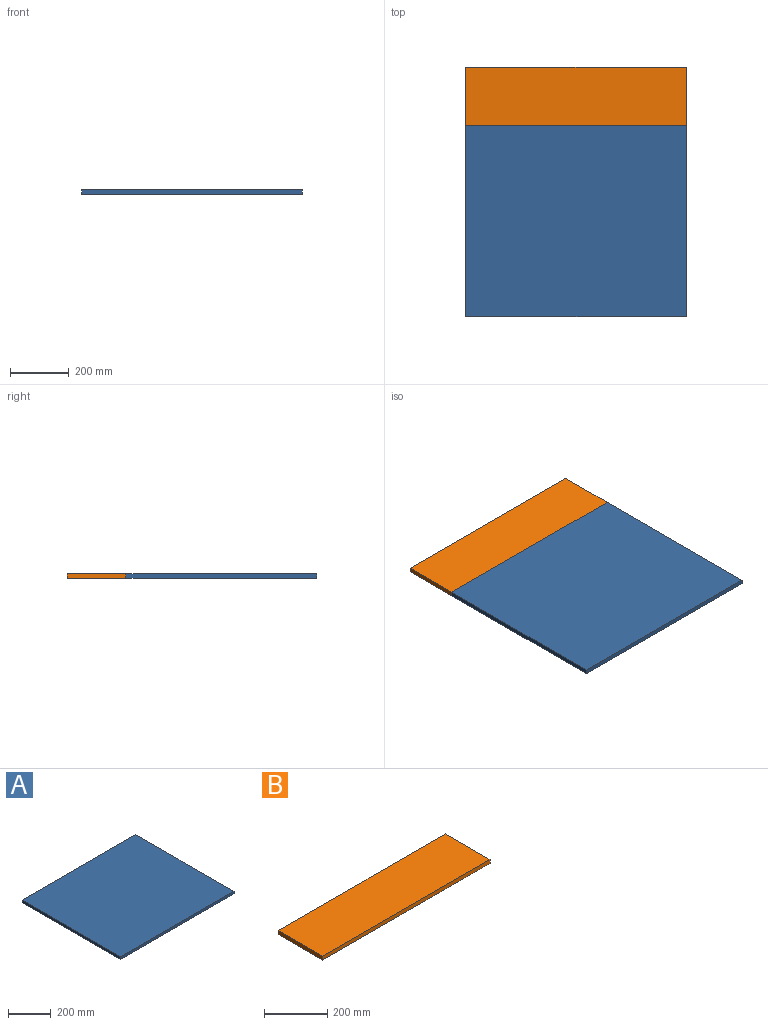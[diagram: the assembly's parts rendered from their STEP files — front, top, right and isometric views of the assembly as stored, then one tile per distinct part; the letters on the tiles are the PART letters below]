
ASSEMBLY  parts=2 mates=1
PART A: 6 faces, bbox 750x650x15 mm
  f0: plane 750x15mm, normal (0,1,0), area 11250mm2, adj f1,f3,f4,f5
  f1: plane 650x15mm, normal (-1,0,0), area 9750mm2, adj f0,f2,f4,f5
  f2: plane 750x15mm, normal (0,-1,0), area 11250mm2, adj f1,f3,f4,f5
  f3: plane 650x15mm, normal (1,0,0), area 9750mm2, adj f0,f2,f4,f5
  f4: plane 750x650mm, normal (0,0,1), area 487500mm2, adj f0,f1,f2,f3
  f5: plane 750x650mm, normal (0,0,-1), area 487500mm2, adj f0,f1,f2,f3
PART B: 6 faces, bbox 750x200x15 mm
  f0: plane 750x15mm, normal (0,1,0), area 11250mm2, adj f1,f3,f4,f5
  f1: plane 200x15mm, normal (-1,0,0), area 3000mm2, adj f0,f2,f4,f5
  f2: plane 750x15mm, normal (0,-1,0), area 11250mm2, adj f1,f3,f4,f5
  f3: plane 200x15mm, normal (1,0,0), area 3000mm2, adj f0,f2,f4,f5
  f4: plane 750x200mm, normal (0,0,1), area 150000mm2, adj f0,f1,f2,f3
  f5: plane 750x200mm, normal (0,0,-1), area 150000mm2, adj f0,f1,f2,f3
PLACE A t=(68.67,-116.02,86.36)mm
PLACE B t=(126.77,130.76,86.36)mm
MATE fastened A.f0 <-> B.f2  axis (0,1,0) through (486.09,189.63,101.36)mm
